# Revit family: Cim 718 LP
name_source: partatom
category: Attrezzatura meccanica
revit_build: Autodesk Revit 2016 (Build: 20160126_1600(x64)
units: mm (PartAtom-declared; Revit-internal decimal feet)

## family parameters
Basato su piano di lavoro = No
Condiviso = No
Numero OmniClass = 23.75.00.00
Punto di calcolo locali = No
Quota connettore circolare = Usa diametro
Sempre verticale = Sì
Taglio con vuoti quando caricato = No
Tipo di parte = Normale
Titolo OmniClass = Climate Control (HVAC)

## types (3) — shared parameters
Descrizione = Differential pressure control valve that maintains constant differential pressure regardless the flow rate.
Fluids = Water and Glycol
Max. differential pressure = 400 kPa
Max. flow temperature = 120°C
Max. static working pressure = 25 bar
Min. temperature = -10°C
Modello = Cim 718 LP
Produttore = Cimberio
Technical Data Sheet = http://web.cimberio.it
URL = http://www.cimberio.it
Δp range = 5-30 kPa

## per-type parameters (varying)
| type | Flow rate | R1 | Technical Code | Weight | c |
| DN 15 1/2"x1/2" | 75-600 l/h | 10 mm  [stored 0.0328084 ft] | DA12501015 | 870   Grms. | 35 mm |
| DN 20 3/4"x3/4" | 100-1250 l/h | 12 mm  [stored 0.0393701 ft] | DA12501020 | 900   Grms. | 36 mm  [stored 0.11811 ft] |
| DN 25 1"x1" | XXX-XXX l/h | 14 mm  [stored 0.0459318 ft] | DA1201025 | 1034   Grms. | 40 mm  [stored 0.131234 ft] |

note: [stored X ft] marks values corroborated as IEEE doubles in the binary element streams (Revit-internal decimal feet)

## geometry (parser evidence)
native form markers: Sweep x12
no freeform markers — native parametric forms only
